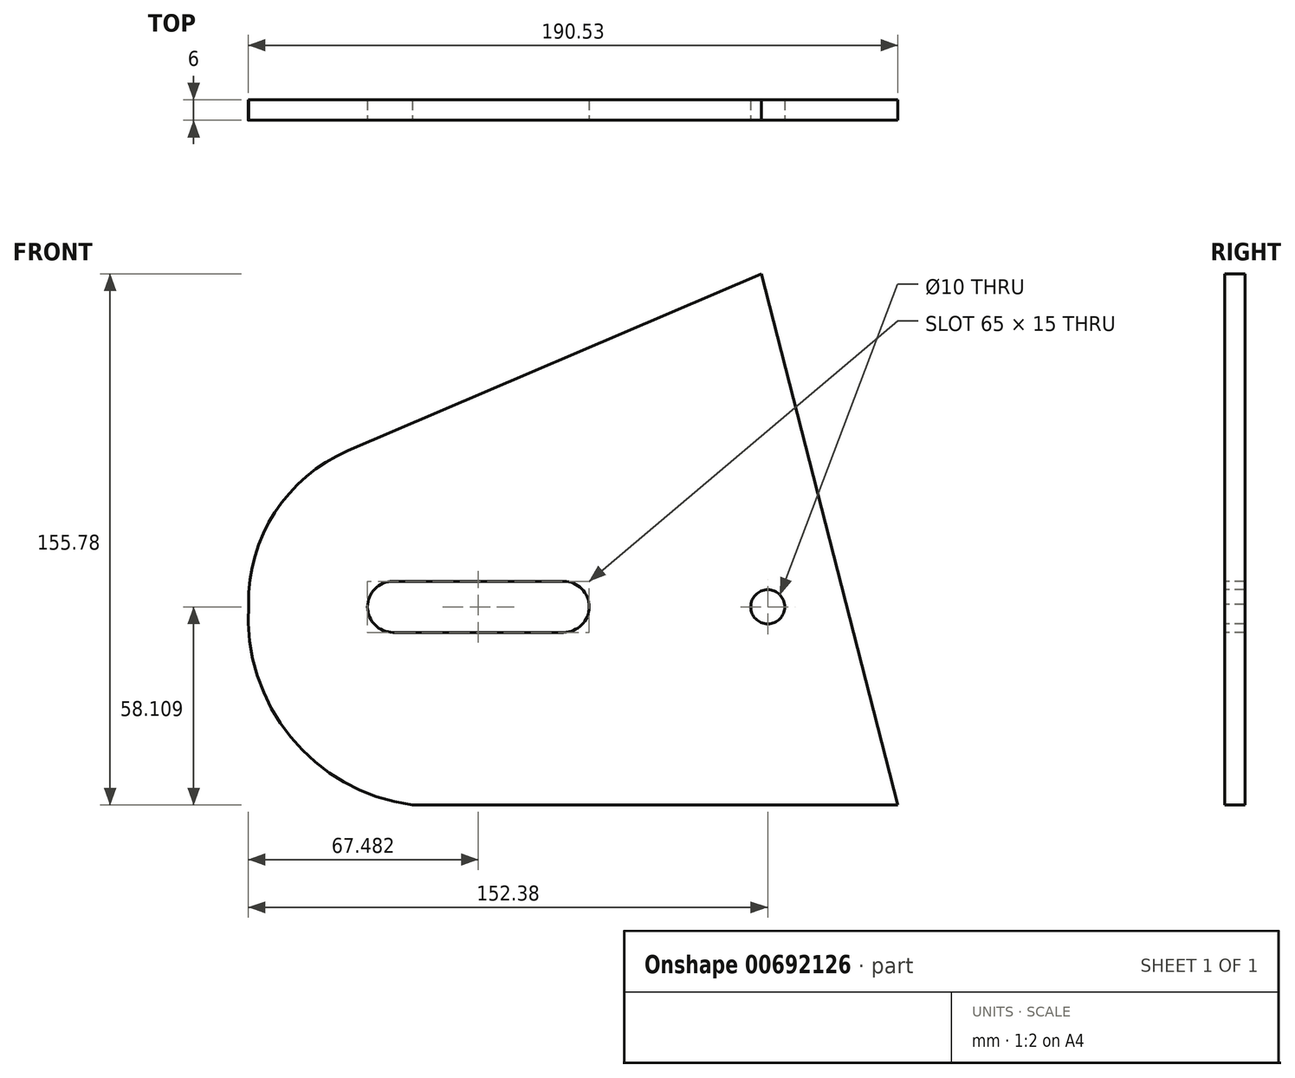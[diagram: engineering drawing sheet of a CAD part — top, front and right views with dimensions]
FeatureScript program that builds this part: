
annotation { "Feature Type Name" : "Feature", "Feature Type Description" : "" }
export const myFeature = defineFeature(function(context is Context, id is Id, definition is map)
    precondition{}
    {
        {
            var Q0;
            Q0=qCreatedBy(makeId("Front.planeOp"),FACE);
            var sketch = newSketch(context, id + "F0", { "sketchPlane" : qUnion([Q0])});
            skLineSegment(sketch, "E0", {"start": v(0, 0) * mm, "end": v(-90, 155.88) * mm});
            skLineSegment(sketch, "E1", {"start": v(0, 0) * mm, "end": v(-173.67, 0) * mm, "construction": true});
            skLineSegment(sketch, "E2", {"start": v(0, 0) * mm, "end": v(215, -372.4) * mm, "construction": true});
            skCircle(sketch, "E3", {"center": v(215, -372.4) * mm, "radius": 295 * mm, "construction": true});
            skLineSegment(sketch, "E4", {"start": v(0, 0) * mm, "end": v(0, -667.4) * mm, "construction": true});
            skLineSegment(sketch, "E5", {"start": v(0, -667.4) * mm, "end": v(-3186.11, -667.4) * mm, "construction": true});
            skLineSegment(sketch, "E6", {"start": v(-3186.11, -667.4) * mm, "end": v(-3186.11, 0) * mm, "construction": true});
            skLineSegment(sketch, "E7", {"start": v(-3186.11, 0) * mm, "end": v(528.5, 0) * mm, "construction": true});
            skCircle(sketch, "E8", {"center": v(-1800, -372.4) * mm, "radius": 295 * mm, "construction": true});
            skLineSegment(sketch, "E9", {"start": v(-45, 77.94) * mm, "end": v(-1703.14, -347.54) * mm, "construction": true});
            skLineSegment(sketch, "E10.0", {"start": v(-76.15, 131.9) * mm, "end": v(-1718.05, -289.42) * mm});
            skLineSegment(sketch, "E11.0", {"start": v(-1675, -277.4) * mm, "end": v(-1925, -277.4) * mm, "construction": true});
            skLineSegment(sketch, "E12.MirrorCS", {"start": v(-1800, -372.4) * mm, "end": v(-1785.09, -430.5) * mm, "construction": true});
            skLineSegment(sketch, "E13.0", {"start": v(-1800, -372.4) * mm, "end": v(-1814.91, -314.27) * mm, "construction": true});
            skLineSegment(sketch, "E14", {"start": v(-1896.86, -397.25) * mm, "end": v(-1896.86, -397.25) * mm});
            skLineSegment(sketch, "E15", {"start": v(-1823.83, -440.45) * mm, "end": v(-1800, -434.33) * mm, "construction": true});
            skLineSegment(sketch, "E16.0", {"start": v(-1703.14, -347.54) * mm, "end": v(-1721.82, -274.72) * mm});
            skLineSegment(sketch, "E17.MirrorCS", {"start": v(-1703.14, -347.54) * mm, "end": v(-1681.85, -430.5) * mm});
            skLineSegment(sketch, "E18", {"start": v(-1782.25, -429.78) * mm, "end": v(-1823.83, -440.45) * mm});
            skPoint(sketch, "E19.visualSharp", {"position": v(-1911.77, -339.13) * mm});
            skPoint(sketch, "E20.visualSharp", {"position": v(-1896.86, -397.25) * mm});
            skPoint(sketch, "E21.visualSharp", {"position": v(-1881.95, -455.36) * mm});
            skLineSegment(sketch, "E22", {"start": v(-1850, -372.4) * mm, "end": v(-1850, -373.27) * mm});
            skLineSegment(sketch, "E23", {"start": v(-1800, -366.4) * mm, "end": v(-1800.01, -366.4) * mm});
            skPoint(sketch, "E24.visualSharp", {"position": v(-1850, -366.4) * mm});
            skPoint(sketch, "E25.visualSharp", {"position": v(-1850, -379.4) * mm});
            skLineSegment(sketch, "E26", {"start": v(-1800, -372.4) * mm, "end": v(-1720, -372.4) * mm, "construction": true});
            skCircle(sketch, "E27", {"center": v(-1720, -372.4) * mm, "radius": 5 * mm});
            skCircle(sketch, "E28", {"center": v(-1812.5, -372.4) * mm, "radius": 100 * mm, "construction": true});
            skLineSegment(sketch, "E29", {"start": v(-1897.92, -372.4) * mm, "end": v(-1250, -372.4) * mm, "construction": true});
            skCircle(sketch, "E30", {"center": v(-1250, -372.4) * mm, "radius": 50 * mm, "construction": true});
            skLineSegment(sketch, "E31", {"start": v(-1250, -372.4) * mm, "end": v(-1077.93, -372.4) * mm, "construction": true});
            skLineSegment(sketch, "E32", {"start": v(-1077.93, -372.4) * mm, "end": v(-1616.42, -372.4) * mm, "construction": true});
            skLineSegment(sketch, "E33", {"start": v(-1077.93, -372.4) * mm, "end": v(-1077.93, -312.4) * mm, "construction": true});
            skLineSegment(sketch, "E34.0", {"start": v(-1327.93, -372.4) * mm, "end": v(-1327.93, -312.4) * mm});
            skLineSegment(sketch, "E35.0", {"start": v(-1327.93, -372.4) * mm, "end": v(-1327.93, -432.4) * mm});
            skLineSegment(sketch, "E36", {"start": v(-1327.93, -432.4) * mm, "end": v(-1077.93, -372.4) * mm});
            skLineSegment(sketch, "E37", {"start": v(-1327.93, -312.4) * mm, "end": v(-1077.93, -372.4) * mm});
            skLineSegment(sketch, "E38.trimOffspring", {"start": v(-1792.42, -432.4) * mm, "end": v(-1785.09, -430.5) * mm, "construction": true});
            skLineSegment(sketch, "E39", {"start": v(-1077.93, -372.4) * mm, "end": v(-1077.93, -249.05) * mm});
            skLineSegment(sketch, "E40", {"start": v(-1327.93, -312.4) * mm, "end": v(-1439.28, 121.55) * mm, "construction": true});
            skLineSegment(sketch, "E41", {"start": v(-1357.56, -196.92) * mm, "end": v(-1361.29, -182.39) * mm});
            skLineSegment(sketch, "E42", {"start": v(-1243, -322.88) * mm, "end": v(-1803.6, -272.79) * mm, "construction": true});
            skLineSegment(sketch, "E43", {"start": v(-1238.68, -421.1) * mm, "end": v(-1803.53, -471.99) * mm, "construction": true});
            skCircle(sketch, "E44", {"center": v(-1327.93, -432.4) * mm, "radius": 10 * mm});
            skCircle(sketch, "E45", {"center": v(-1327.93, -312.4) * mm, "radius": 10 * mm});
            skCircle(sketch, "E46.0", {"center": v(-1327.93, -432.4) * mm, "radius": 8 * mm});
            skCircle(sketch, "E47.0", {"center": v(-1327.93, -312.4) * mm, "radius": 8 * mm});
            skLineSegment(sketch, "E48", {"start": v(-1357.56, -196.92) * mm, "end": v(-1327.93, -312.4) * mm});
            skLineSegment(sketch, "E49", {"start": v(-1357.56, -196.92) * mm, "end": v(-874.75, -196.92) * mm});
            skLineSegment(sketch, "E50", {"start": v(-13.85, 24) * mm, "end": v(-496.66, 24) * mm});
            skLineSegment(sketch, "E51", {"start": v(-496.66, 24) * mm, "end": v(-874.75, -196.92) * mm});
            skLineSegment(sketch, "E52", {"start": v(-1688.23, -405.65) * mm, "end": v(-1357.56, -196.92) * mm});
            skCircle(sketch, "E53", {"center": v(-1077.93, -372.4) * mm, "radius": 10 * mm});
            skCircle(sketch, "E54.0", {"center": v(-1077.93, -372.4) * mm, "radius": 8 * mm});
            skLineSegment(sketch, "E55", {"start": v(-1327.93, -313.2) * mm, "end": v(-1337.89, -312.31) * mm});
            skPoint(sketch, "E56.visualSharp", {"position": v(-1839.73, -379.4) * mm});
            skPoint(sketch, "E57.visualSharp", {"position": v(-1839.73, -365.4) * mm});
            skPoint(sketch, "E58.visualSharp", {"position": v(-1759.73, -379.4) * mm});
            skPoint(sketch, "E59.newPointA", {"position": v(-1759.73, -367.4) * mm});
            skPoint(sketch, "E59.newPointB", {"position": v(-1759.73, -365.4) * mm});
            skLineSegment(sketch, "E60.0", {"start": v(-1760.01, -372.4) * mm, "end": v(-1760.01, -372.4) * mm});
            skPoint(sketch, "E61.newPointA", {"position": v(-1840.01, -378.4) * mm});
            skPoint(sketch, "E61.newPointB", {"position": v(-1897.92, -378.4) * mm});
            skPoint(sketch, "E62.newPointA", {"position": v(-1840.01, -366.4) * mm});
            skPoint(sketch, "E62.newPointB", {"position": v(-1897.92, -366.4) * mm});
            skPoint(sketch, "E63.newPointA", {"position": v(-1760.01, -366.4) * mm});
            skPoint(sketch, "E63.newPointB", {"position": v(-1250, -366.4) * mm});
            skPoint(sketch, "E64.visualSharp", {"position": v(-1760.01, -372.4) * mm});
            skPoint(sketch, "E65.newPointA", {"position": v(-1250, -378.4) * mm});
            skPoint(sketch, "E65.newPointB", {"position": v(-1760.01, -378.4) * mm});
            skLineSegment(sketch, "E66.trimOffspring", {"start": v(-1746.1, -420.5) * mm, "end": v(-1782.25, -429.78) * mm});
            skLineSegment(sketch, "E67.trimOffspring", {"start": v(-1776.62, -366.4) * mm, "end": v(-1800, -372.4) * mm, "construction": true});
            skLineSegment(sketch, "E68", {"start": v(-1718.05, -289.42) * mm, "end": v(-76.15, 131.9) * mm});
            skLineSegment(sketch, "E69", {"start": v(-13.85, 24) * mm, "end": v(-1688.23, -405.65) * mm});
            skLineSegment(sketch, "E70", {"start": v(-1688.23, -405.65) * mm, "end": v(-1327.93, -432.4) * mm});
            skPoint(sketch, "E71.visualSharp", {"position": v(-1900.1, -367.32) * mm});
            skLineSegment(sketch, "E72.0", {"start": v(-1915.1, -405.65) * mm, "end": v(-1915.1, -377.22) * mm});
            skLineSegment(sketch, "E73.0", {"start": v(-1852.26, -372.65) * mm, "end": v(-1852.26, -372.4) * mm});
            skPoint(sketch, "E74.orphan", {"position": v(-1854.9, -405.65) * mm});
            skPoint(sketch, "E75.end.orphan", {"position": v(-1854.9, -372.4) * mm});
            skPoint(sketch, "E76.visualSharp", {"position": v(-1852.26, -405.65) * mm});
            skPoint(sketch, "E77.visualSharp", {"position": v(-1852.26, -346.85) * mm});
            skPoint(sketch, "E78.orphan", {"position": v(-1852.26, -372.4) * mm});
            skLineSegment(sketch, "E79.0", {"start": v(-1857.26, -372.65) * mm, "end": v(-1857.26, -370.77) * mm});
            skPoint(sketch, "E80.visualSharp", {"position": v(-1857.26, -405.65) * mm});
            skLineSegment(sketch, "E81.0", {"start": v(-1843.14, -326.64) * mm, "end": v(-1721.82, -274.72) * mm});
            skArc(sketch, "E82.0", {"start": v(-1843.14, -326.64) * mm, "mid": v(-1864.77, -345.01) * mm, "end": v(-1872.23, -372.4) * mm});
            skArc(sketch, "E83.converted", {"start": v(-1872.25, -371.7) * mm, "mid": v(-1872.26, -372.05) * mm, "end": v(-1872.26, -372.4) * mm});
            skLineSegment(sketch, "E84", {"start": v(-1829.9, -372.4) * mm, "end": v(-1779.9, -372.4) * mm, "construction": true});
            skLineSegment(sketch, "E85.0", {"start": v(-1829.9, -364.9) * mm, "end": v(-1779.9, -364.9) * mm});
            skLineSegment(sketch, "E86.0", {"start": v(-1829.9, -379.9) * mm, "end": v(-1779.9, -379.9) * mm});
            skArc(sketch, "E87", {"start": v(-1779.9, -379.9) * mm, "mid": v(-1772.4, -372.4) * mm, "end": v(-1779.9, -364.9) * mm});
            skArc(sketch, "E88", {"start": v(-1829.9, -364.9) * mm, "mid": v(-1837.4, -372.4) * mm, "end": v(-1829.9, -379.9) * mm});
            skLineSegment(sketch, "E89.0", {"start": v(-1684.38, -420.5) * mm, "end": v(-1684.41, -420.5) * mm});
            skLineSegment(sketch, "E90.0", {"start": v(-1681.85, -430.5) * mm, "end": v(-1824.26, -430.5) * mm});
            skArc(sketch, "E91", {"start": v(-1872.25, -371.7) * mm, "mid": v(-1859.88, -410.6) * mm, "end": v(-1824.26, -430.5) * mm});
            skArc(sketch, "E92.trimOffspring", {"start": v(-1784.65, -420.65) * mm, "mid": v(-1784.54, -420.58) * mm, "end": v(-1784.44, -420.5) * mm});
            skLineSegment(sketch, "E93.trimOffspring", {"start": v(-1784.44, -420.5) * mm, "end": v(-1787.65, -420.5) * mm});
            skLineSegment(sketch, "E94.trimOffspring", {"start": v(-1724.83, -420.5) * mm, "end": v(-1746.1, -420.5) * mm});
            skPoint(sketch, "E95.orphan", {"position": v(-1721.68, -414.24) * mm});
            skLineSegment(sketch, "E96.0", {"start": v(-78.5, 141.1) * mm, "end": v(-1756.03, -289.36) * mm, "construction": true});
            skLineSegment(sketch, "E97.MirrorCS", {"start": v(-73.79, 122.7) * mm, "end": v(-1715.69, -298.62) * mm, "construction": true});
            skPoint(sketch, "E98.orphan", {"position": v(-1720.41, -280.22) * mm});
            skSolve(sketch);
        }
        {
            var Q0;
            Q0=makeQuery(id+"F0.imprint","IMPRINT",FACE,{"disambiguationData":[TD([[makeQuery(id+"F0.imprint","IMPRINT",EDGE,{"derivedFrom":sQuery(id+"F0.wireOp",EDGE,"E16.0")}),1.0]])]});
            extrude(context, id + "F1", {"entities" : qUnion([Q0]), "oppositeDirection" : true, "depth" : 6 * mm, "offsetDistance" : 25 * mm});
        }
    });
